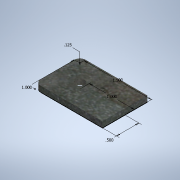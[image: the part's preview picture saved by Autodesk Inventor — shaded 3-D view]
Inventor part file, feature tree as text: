
AUTODESK INVENTOR PART (.ipt)
format: ipt  version: 2021 (Build 250183000, 183)  size: 120,320 bytes
history: native  units: in
note: dims shown in document units (in); Inventor stores cm internally (conversion verified against a paired STEP export)
features: sketch x1, extrude x1, hole x1
ambient origin geometry x8: Origin, YZ Plane, XZ Plane, XY Plane, X Axis, Y Axis, Z Axis, Center Point
bodies: Solid1 (feature_tree)
feature tree (3):
  sketch  "Sketch1"  dims[d0=1.5in d1=1.0in d2=0.5in d3=1.0in d5=0.125in d6=0.0in d7=0.125in d8=0.201in d9=0.75in d10=0.385in d11=0.25in d12=0.5635in d13=1.0in d14=0.8108in]
  extrude  "Extrusion1"  Depth=1.0in
  hole  "Hole1"  [1 undecoded]
note: 1 required parameter value undecoded (feature->parameter linkage not recoverable at this tier; creation-order binding heuristic only, values carry confidence <= 0.55)
